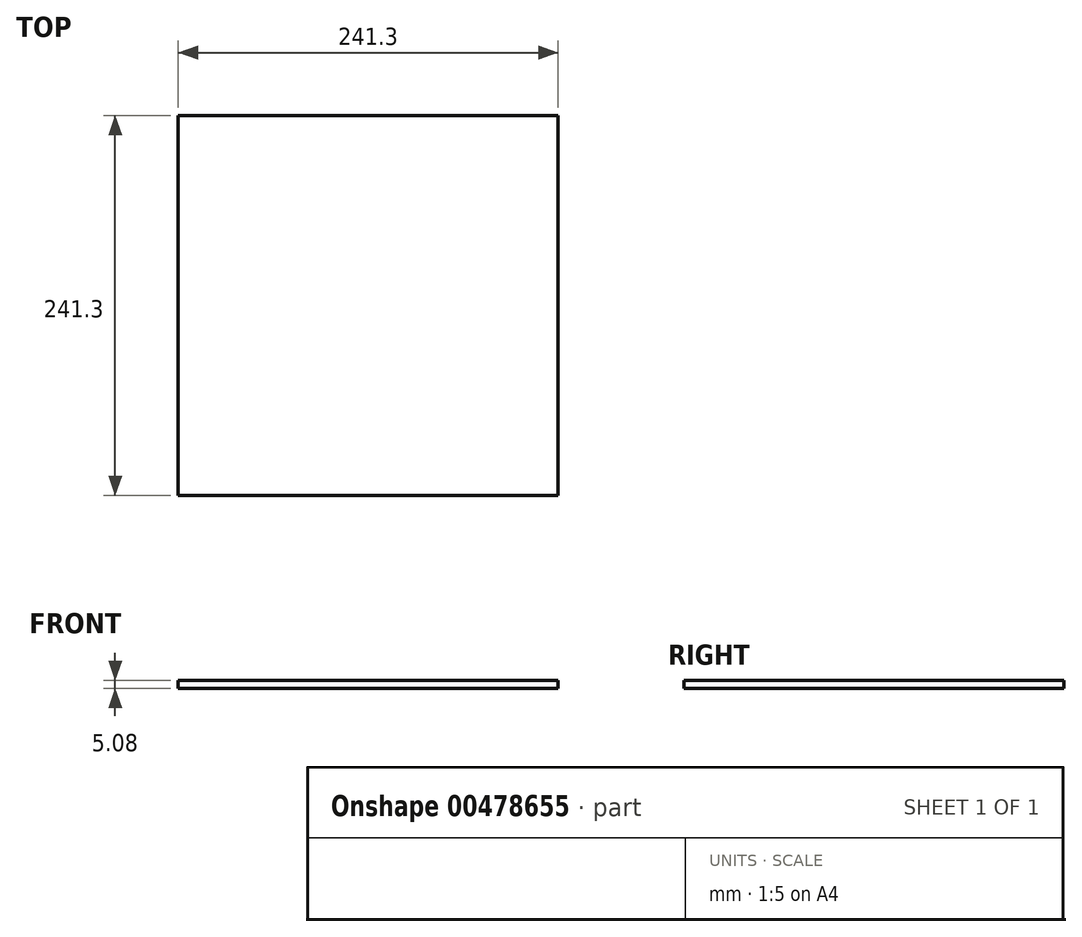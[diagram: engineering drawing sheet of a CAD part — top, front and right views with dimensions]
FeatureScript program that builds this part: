
annotation { "Feature Type Name" : "Feature", "Feature Type Description" : "" }
export const myFeature = defineFeature(function(context is Context, id is Id, definition is map)
    precondition{}
    {
        {
            var Q0;
            Q0=qCreatedBy(makeId("Top.planeOp"),FACE);
            var sketch = newSketch(context, id + "F0", { "sketchPlane" : qUnion([Q0])});
            skLineSegment(sketch, "E0.bottom", {"start": v(120.65, 120.65) * mm, "end": v(-120.65, 120.65) * mm});
            skLineSegment(sketch, "E0.top", {"start": v(120.65, -120.65) * mm, "end": v(-120.65, -120.65) * mm});
            skLineSegment(sketch, "E0.left", {"start": v(120.65, 120.65) * mm, "end": v(120.65, -120.65) * mm});
            skLineSegment(sketch, "E0.right", {"start": v(-120.65, 120.65) * mm, "end": v(-120.65, -120.65) * mm});
            skPoint(sketch, "E0.middle", {"position": v(0, 0) * mm});
            skSolve(sketch);
        }
        {
            var Q0;
            Q0=makeQuery(id+"F0.imprint","IMPRINT",FACE,{"disambiguationData":[TD([[makeQuery(id+"F0.imprint","IMPRINT",EDGE,{"derivedFrom":sQuery(id+"F0.wireOp",EDGE,"E0.bottom")}),1.0]])]});
            extrude(context, id + "F1", {"entities" : qUnion([Q0]), "depth" : 5.08 * mm});
        }
    });
